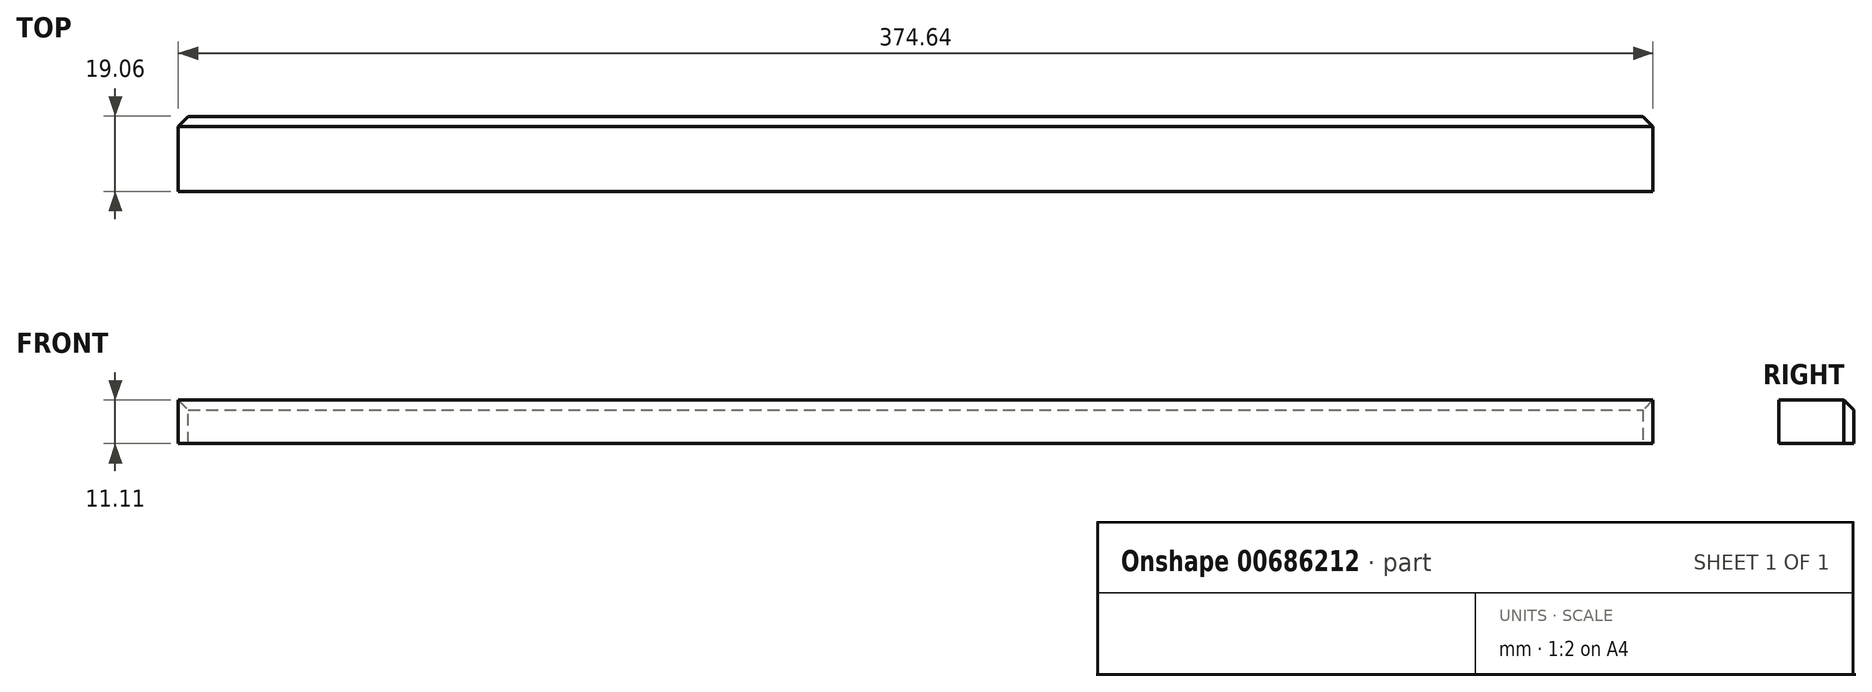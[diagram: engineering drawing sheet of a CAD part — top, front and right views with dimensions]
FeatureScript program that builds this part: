
annotation { "Feature Type Name" : "Feature", "Feature Type Description" : "" }
export const myFeature = defineFeature(function(context is Context, id is Id, definition is map)
    precondition{}
    {
        {
            var Q0;
            Q0=qCreatedBy(makeId("Top.planeOp"),FACE);
            var sketch = newSketch(context, id + "F0", { "sketchPlane" : qUnion([Q0])});
            skLineSegment(sketch, "E0.bottom", {"start": v(-187.33, 9.52) * mm, "end": v(187.32, 9.52) * mm});
            skLineSegment(sketch, "E0.top", {"start": v(-187.33, -9.53) * mm, "end": v(187.32, -9.53) * mm});
            skLineSegment(sketch, "E0.left", {"start": v(-187.33, 9.53) * mm, "end": v(-187.33, -9.53) * mm});
            skLineSegment(sketch, "E0.right", {"start": v(187.32, 9.53) * mm, "end": v(187.32, -9.53) * mm});
            skPoint(sketch, "E0.middle", {"position": v(0, 0) * mm});
            skSolve(sketch);
        }
        {
            var Q0;
            Q0=makeQuery(id+"F0.imprint","IMPRINT",FACE,{"disambiguationData":[TD([[makeQuery(id+"F0.imprint","IMPRINT",EDGE,{"derivedFrom":sQuery(id+"F0.wireOp",EDGE,"E0.bottom")}),-1.0]])]});
            extrude(context, id + "F1", {"entities" : qUnion([Q0]), "depth" : 11.1 * mm, "offsetDistance" : 25.4 * mm});
        }
        {
            var Q0;
            Q0=makeQuery(id+"F1.opExtrude","CAP_EDGE",EDGE,{"disambiguationData":[OSD([sQuery(id+"F0.wireOp",EDGE,"E0.bottom")])],"isStart":false});
            var Q1;
            Q1=makeQuery(id+"F1.opExtrude","SWEPT_EDGE",EDGE,{"disambiguationData":[OSD([sQuery(id+"F0.wireOp",EDGE,"E0.bottom"),sQuery(id+"F0.wireOp",EDGE,"E0.right")])]});
            var Q2;
            Q2=makeQuery(id+"F1.opExtrude","SWEPT_EDGE",EDGE,{"disambiguationData":[OSD([sQuery(id+"F0.wireOp",EDGE,"E0.bottom"),sQuery(id+"F0.wireOp",EDGE,"E0.left")])]});
            chamfer(context, id + "F2", {"entities" : qUnion([Q0, Q1, Q2]), "width" : 2.54 * mm, "tangentPropagation" : true});
        }
    });
